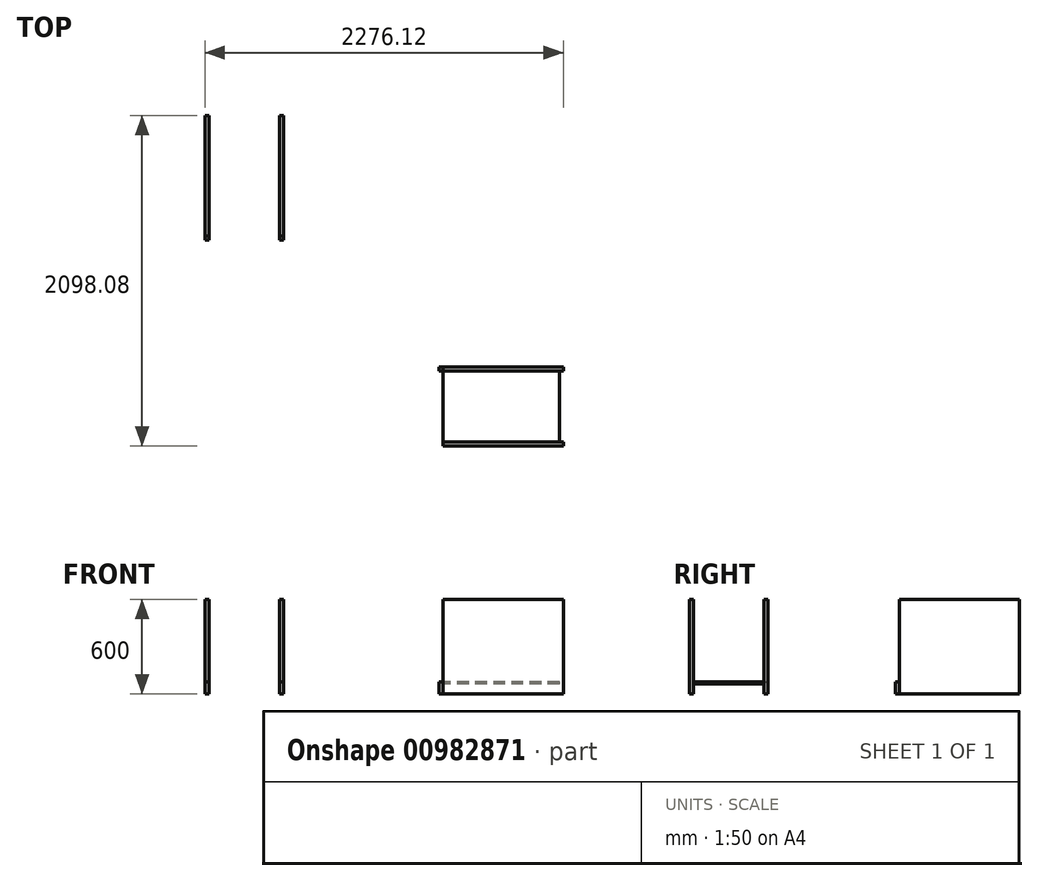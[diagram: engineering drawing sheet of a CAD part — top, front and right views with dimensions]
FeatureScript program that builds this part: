
annotation { "Feature Type Name" : "Feature", "Feature Type Description" : "" }
export const myFeature = defineFeature(function(context is Context, id is Id, definition is map)
    precondition{}
    {
        {
            var Q0;
            Q0=qCreatedBy(makeId("Top.planeOp"),FACE);
            var sketch = newSketch(context, id + "F0", { "sketchPlane" : qUnion([Q0])});
            skLineSegment(sketch, "E0.left", {"start": v(-1401.2, 542.37) * mm, "end": v(-1401.2, 242.37) * mm});
            skLineSegment(sketch, "E1.bottom", {"start": v(254.9, -1235.71) * mm, "end": v(554.9, -1235.71) * mm});
            skLineSegment(sketch, "E2.bottom", {"start": v(-1426.2, 837.37) * mm, "end": v(-1401.2, 837.37) * mm});
            skLineSegment(sketch, "E2.top", {"start": v(-1426.2, 47.37) * mm, "end": v(-1401.2, 47.37) * mm});
            skLineSegment(sketch, "E2.left", {"start": v(-1426.2, 837.37) * mm, "end": v(-1426.2, 47.37) * mm});
            skLineSegment(sketch, "E2.right", {"start": v(-1401.2, 837.37) * mm, "end": v(-1401.2, 47.37) * mm});
            skLineSegment(sketch, "E3.left", {"start": v(-1401.2, 47.37) * mm, "end": v(-1401.2, 72.37) * mm});
            skLineSegment(sketch, "E4.left", {"start": v(-1401.2, 837.37) * mm, "end": v(-1401.2, 812.37) * mm});
            skLineSegment(sketch, "E5", {"start": v(254.9, -1235.71) * mm, "end": v(59.9, -1235.71) * mm});
            skLineSegment(sketch, "E6", {"start": v(59.9, -1235.71) * mm, "end": v(59.9, -1260.71) * mm});
            skLineSegment(sketch, "E7", {"start": v(59.9, -1260.71) * mm, "end": v(849.9, -1260.71) * mm});
            skLineSegment(sketch, "E8", {"start": v(849.9, -1260.71) * mm, "end": v(849.9, -1235.71) * mm});
            skLineSegment(sketch, "E9", {"start": v(849.9, -1235.71) * mm, "end": v(554.9, -1235.71) * mm});
            skLineSegment(sketch, "E10.bottom", {"start": v(59.9, -1235.71) * mm, "end": v(84.9, -1235.71) * mm});
            skLineSegment(sketch, "E11.bottom", {"start": v(849.9, -1235.71) * mm, "end": v(824.9, -1235.71) * mm});
            skLineSegment(sketch, "E12.top", {"start": v(292.4, -1260.71) * mm, "end": v(317.4, -1260.71) * mm});
            skLineSegment(sketch, "E13.top", {"start": v(592.4, -1260.71) * mm, "end": v(617.4, -1260.71) * mm});
            skLineSegment(sketch, "E14", {"start": v(-951.2, 47.37) * mm, "end": v(-951.2, 837.37) * mm});
            skLineSegment(sketch, "E15", {"start": v(-926.2, 837.37) * mm, "end": v(-926.2, 47.37) * mm});
            skLineSegment(sketch, "E16", {"start": v(59.9, -760.71) * mm, "end": v(849.9, -760.71) * mm});
            skLineSegment(sketch, "E17", {"start": v(59.9, -785.71) * mm, "end": v(849.9, -785.71) * mm});
            skLineSegment(sketch, "E18", {"start": v(-1401.2, 812.37) * mm, "end": v(-926.2, 812.37) * mm});
            skLineSegment(sketch, "E19", {"start": v(-1401.2, 72.37) * mm, "end": v(-926.2, 72.37) * mm});
            skLineSegment(sketch, "E20", {"start": v(-1401.2, 47.37) * mm, "end": v(-926.2, 47.37) * mm});
            skLineSegment(sketch, "E21", {"start": v(-1401.2, 837.37) * mm, "end": v(-926.2, 837.37) * mm});
            skLineSegment(sketch, "E22", {"start": v(59.9, -760.71) * mm, "end": v(59.9, -1260.71) * mm});
            skLineSegment(sketch, "E23", {"start": v(849.9, -1260.71) * mm, "end": v(849.9, -760.71) * mm});
            skLineSegment(sketch, "E24", {"start": v(84.9, -1235.71) * mm, "end": v(84.9, -760.71) * mm});
            skLineSegment(sketch, "E25", {"start": v(824.9, -1235.71) * mm, "end": v(824.9, -760.71) * mm});
            skLineSegment(sketch, "E26", {"start": v(-1401.2, 72.37) * mm, "end": v(-1426.2, 72.37) * mm});
            skLineSegment(sketch, "E27", {"start": v(84.9, -1235.71) * mm, "end": v(84.9, -1260.71) * mm});
            skSolve(sketch);
        }
        {
            var Q0;
            {var subQ0=sQuery(id+"F0.wireOp",EDGE,"E21");var subQ1=sQuery(id+"F0.wireOp",EDGE,"E14");var subQ2=makeQuery(id+"F0.imprint","INTERSECT",VERTEX,{"derivedFrom":[subQ1,subQ0]});Q0=makeQuery(id+"F0.imprint","IMPRINT",FACE,{"disambiguationData":[TD([[makeQuery(id+"F0.imprint","IMPRINT",EDGE,{"disambiguationData":[TD([[subQ2,1.0]])],"derivedFrom":subQ1}),-1.0]])]});}
            var Q1;
            {var subQ0=sQuery(id+"F0.wireOp",EDGE,"E23");var subQ1=sQuery(id+"F0.wireOp",EDGE,"E16");var subQ2=makeQuery(id+"F0.imprint","INTERSECT",VERTEX,{"derivedFrom":[subQ1,subQ0]});Q1=makeQuery(id+"F0.imprint","IMPRINT",FACE,{"disambiguationData":[TD([[makeQuery(id+"F0.imprint","IMPRINT",EDGE,{"disambiguationData":[TD([[subQ2,1.0]])],"derivedFrom":subQ1}),-1.0]])]});}
            var Q2;
            Q2=makeQuery(id+"F0.imprint","IMPRINT",FACE,{"disambiguationData":[TD([[makeQuery(id+"F0.imprint","IMPRINT",EDGE,{"derivedFrom":sQuery(id+"F0.wireOp",EDGE,"E1.bottom")}),-1.0]])]});
            var Q3;
            {var subQ4=sQuery(id+"F0.wireOp",EDGE,"E2.bottom");Q3=makeQuery(id+"F0.imprint","IMPRINT",FACE,{"disambiguationData":[TD([[makeQuery(id+"F0.imprint","IMPRINT",EDGE,{"derivedFrom":subQ4}),-1.0]])]});}
            var Q4;
            {var subQ0=sQuery(id+"F0.wireOp",EDGE,"E4.left");Q4=makeQuery(id+"F0.imprint","IMPRINT",FACE,{"disambiguationData":[TD([[makeQuery(id+"F0.imprint","IMPRINT",EDGE,{"derivedFrom":subQ0}),1.0]])]});}
            var Q5;
            {var subQ0=sQuery(id+"F0.wireOp",EDGE,"E11.bottom");Q5=makeQuery(id+"F0.imprint","IMPRINT",FACE,{"disambiguationData":[TD([[makeQuery(id+"F0.imprint","IMPRINT",EDGE,{"derivedFrom":subQ0}),-1.0]])]});}
            var Q6;
            {var subQ0=sQuery(id+"F0.wireOp",EDGE,"E19");var subQ1=sQuery(id+"F0.wireOp",EDGE,"E14");var subQ2=makeQuery(id+"F0.imprint","INTERSECT",VERTEX,{"derivedFrom":[subQ1,subQ0]});Q6=makeQuery(id+"F0.imprint","IMPRINT",FACE,{"disambiguationData":[TD([[makeQuery(id+"F0.imprint","IMPRINT",EDGE,{"disambiguationData":[TD([[subQ2,-1.0]])],"derivedFrom":subQ1}),-1.0]])]});}
            var Q7;
            {var subQ0=sQuery(id+"F0.wireOp",EDGE,"E24");var subQ1=sQuery(id+"F0.wireOp",EDGE,"E16");var subQ2=makeQuery(id+"F0.imprint","INTERSECT",VERTEX,{"derivedFrom":[subQ1,subQ0]});Q7=makeQuery(id+"F0.imprint","IMPRINT",FACE,{"disambiguationData":[TD([[makeQuery(id+"F0.imprint","IMPRINT",EDGE,{"disambiguationData":[TD([[subQ2,-1.0]])],"derivedFrom":subQ1}),-1.0]])]});}
            extrude(context, id + "F1", {"entities" : qUnion([Q0, Q1, Q2, Q3, Q4, Q5, Q6, Q7]), "depth" : 525 * mm, "offsetDistance" : 25 * mm, "hasSecondDirection" : true, "secondDirectionOppositeDirection" : true, "secondDirectionDepth" : 75 * mm});
        }
        {
            var Q0;
            {var subQ0=sQuery(id+"F0.wireOp",EDGE,"E2.top");Q0=makeQuery(id+"F0.imprint","IMPRINT",FACE,{"disambiguationData":[TD([[makeQuery(id+"F0.imprint","IMPRINT",EDGE,{"derivedFrom":subQ0}),1.0]])]});}
            var Q1;
            {var subQ0=sQuery(id+"F0.wireOp",EDGE,"E3.left");Q1=makeQuery(id+"F0.imprint","IMPRINT",FACE,{"disambiguationData":[TD([[makeQuery(id+"F0.imprint","IMPRINT",EDGE,{"derivedFrom":subQ0}),-1.0]])]});}
            var Q2;
            {var subQ0=sQuery(id+"F0.wireOp",EDGE,"E20");var subQ1=sQuery(id+"F0.wireOp",EDGE,"E14");var subQ2=makeQuery(id+"F0.imprint","INTERSECT",VERTEX,{"derivedFrom":[subQ1,subQ0]});Q2=makeQuery(id+"F0.imprint","IMPRINT",FACE,{"disambiguationData":[TD([[makeQuery(id+"F0.imprint","IMPRINT",EDGE,{"disambiguationData":[TD([[subQ2,-1.0]])],"derivedFrom":subQ1}),-1.0]])]});}
            var Q3;
            {var subQ0=sQuery(id+"F0.wireOp",EDGE,"E22");var subQ1=sQuery(id+"F0.wireOp",EDGE,"E16");var subQ2=makeQuery(id+"F0.imprint","INTERSECT",VERTEX,{"derivedFrom":[subQ1,subQ0]});Q3=makeQuery(id+"F0.imprint","IMPRINT",FACE,{"disambiguationData":[TD([[makeQuery(id+"F0.imprint","IMPRINT",EDGE,{"disambiguationData":[TD([[subQ2,-1.0]])],"derivedFrom":subQ1}),-1.0]])]});}
            var Q4;
            {var subQ0=sQuery(id+"F0.wireOp",EDGE,"E10.bottom");Q4=makeQuery(id+"F0.imprint","IMPRINT",FACE,{"disambiguationData":[TD([[makeQuery(id+"F0.imprint","IMPRINT",EDGE,{"derivedFrom":subQ0}),1.0]])]});}
            var Q5;
            {var subQ4=sQuery(id+"F0.wireOp",EDGE,"E10.bottom");Q5=makeQuery(id+"F0.imprint","IMPRINT",FACE,{"disambiguationData":[TD([[makeQuery(id+"F0.imprint","IMPRINT",EDGE,{"derivedFrom":subQ4}),-1.0]])]});}
            extrude(context, id + "F2", {"entities" : qUnion([Q0, Q1, Q2, Q3, Q4, Q5]), "depth" : 0 * mm, "offsetDistance" : 25 * mm, "hasSecondDirection" : true, "secondDirectionOppositeDirection" : true, "secondDirectionDepth" : 75 * mm});
        }
        {
            var Q0;
            Q0=makeQuery(id+"F0.imprint","IMPRINT",FACE,{"disambiguationData":[TD([[makeQuery(id+"F0.imprint","IMPRINT",EDGE,{"derivedFrom":sQuery(id+"F0.wireOp",EDGE,"E1.bottom")}),1.0]])]});
            var Q1;
            {var subQ1=sQuery(id+"F0.wireOp",EDGE,"E2.right");var subQ9=makeQuery(id+"F0.imprint","IMPRINT",VERTEX,{"disambiguationData":[OD(0.0)],"derivedFrom":subQ1});Q1=makeQuery(id+"F0.imprint","IMPRINT",FACE,{"disambiguationData":[TD([[makeQuery(id+"F0.imprint","IMPRINT",EDGE,{"disambiguationData":[TD([[subQ9,-1.0]])],"derivedFrom":subQ1}),1.0]])]});}
            extrude(context, id + "F3", {"entities" : qUnion([Q0, Q1]), "operationType" : NewBodyOperationType.ADD, "depth" : 0 * mm, "offsetDistance" : 25 * mm, "hasSecondDirection" : true, "secondDirectionOppositeDirection" : true, "secondDirectionDepth" : 10 * mm});
        }
    });
